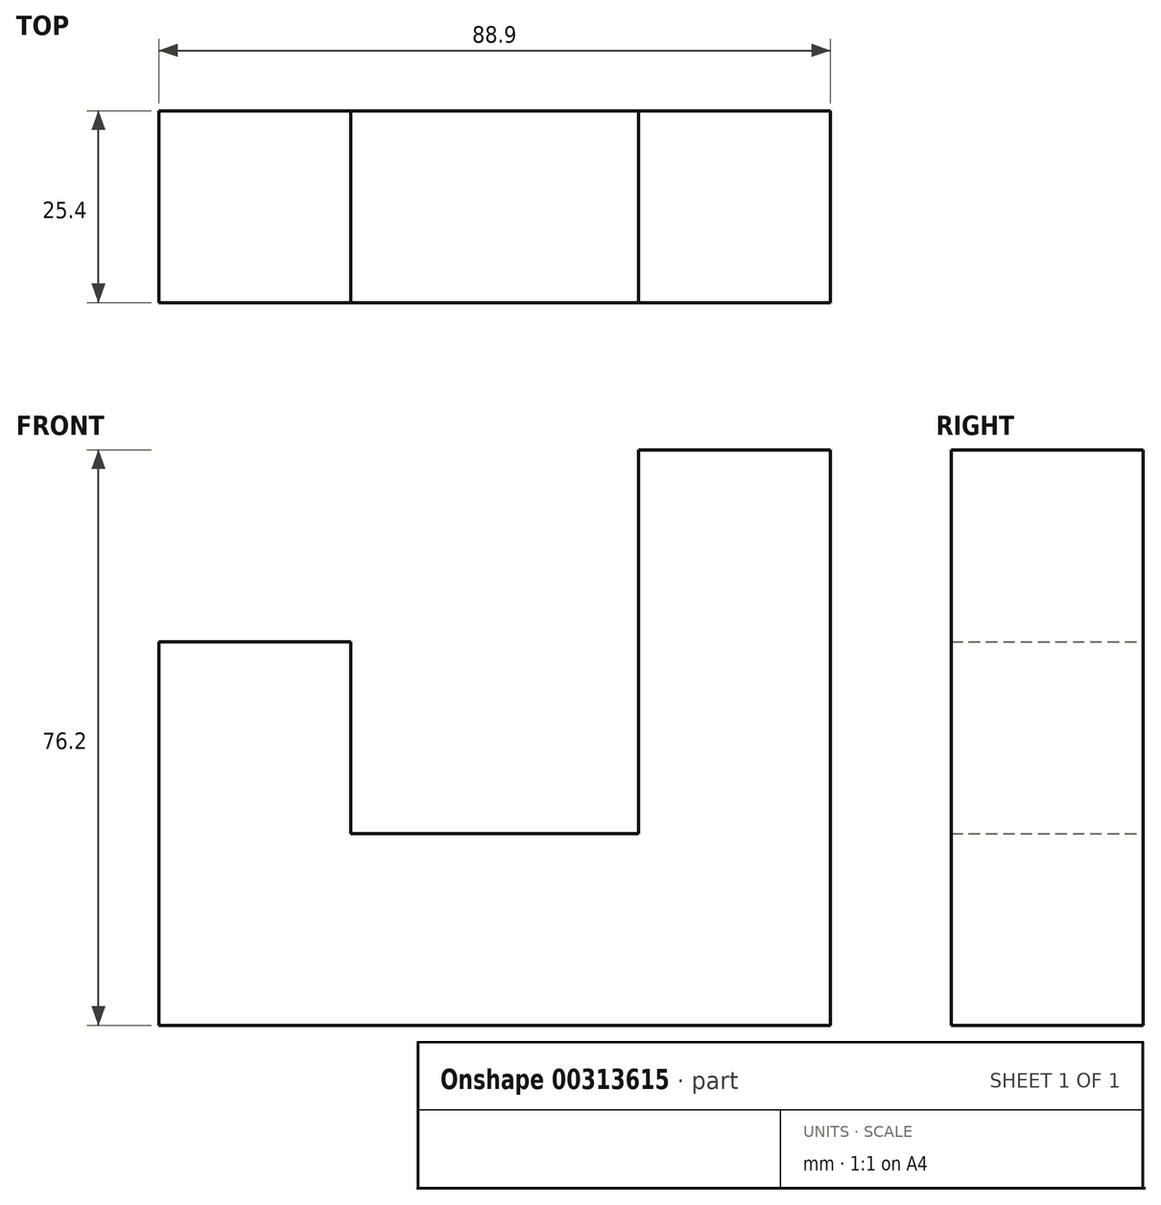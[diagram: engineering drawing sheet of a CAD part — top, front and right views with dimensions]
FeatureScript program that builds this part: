
annotation { "Feature Type Name" : "Feature", "Feature Type Description" : "" }
export const myFeature = defineFeature(function(context is Context, id is Id, definition is map)
    precondition{}
    {
        {
            var Q0;
            Q0=qCreatedBy(makeId("Front.planeOp"),FACE);
            var sketch = newSketch(context, id + "F0", { "sketchPlane" : qUnion([Q0])});
            skLineSegment(sketch, "E0", {"start": v(-35.92, -45.34) * mm, "end": v(52.98, -45.34) * mm});
            skLineSegment(sketch, "E1", {"start": v(52.98, -45.34) * mm, "end": v(52.98, 30.86) * mm});
            skLineSegment(sketch, "E2", {"start": v(52.98, 30.86) * mm, "end": v(27.58, 30.86) * mm});
            skLineSegment(sketch, "E3", {"start": v(27.58, 30.86) * mm, "end": v(27.58, -19.94) * mm});
            skLineSegment(sketch, "E4", {"start": v(27.58, -19.94) * mm, "end": v(-10.52, -19.94) * mm});
            skLineSegment(sketch, "E5", {"start": v(-10.52, -19.94) * mm, "end": v(-10.52, 5.46) * mm});
            skLineSegment(sketch, "E6", {"start": v(-10.52, 5.46) * mm, "end": v(-35.92, 5.46) * mm});
            skLineSegment(sketch, "E7", {"start": v(-35.92, 5.46) * mm, "end": v(-35.92, -45.34) * mm});
            skSolve(sketch);
        }
        {
            var Q0;
            Q0=makeQuery(id+"F0.imprint","IMPRINT",FACE,{"disambiguationData":[TD([[makeQuery(id+"F0.imprint","IMPRINT",EDGE,{"derivedFrom":sQuery(id+"F0.wireOp",EDGE,"E0")}),1.0]])]});
            extrude(context, id + "F1", {"entities" : qUnion([Q0]), "depth" : 25.4 * mm});
        }
    });
